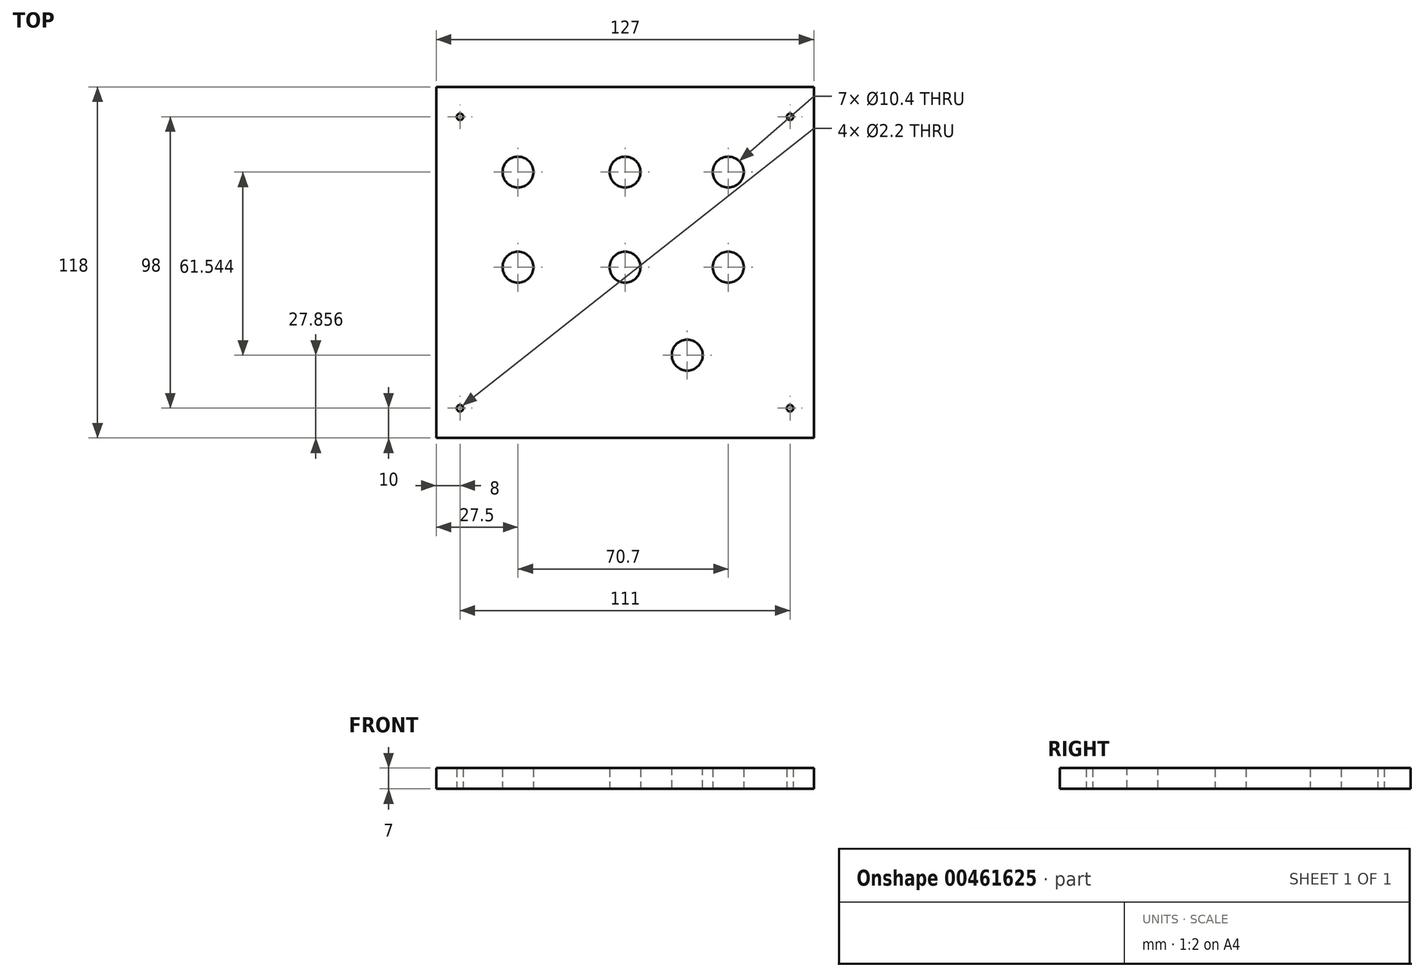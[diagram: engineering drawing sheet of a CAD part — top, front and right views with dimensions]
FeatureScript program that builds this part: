
annotation { "Feature Type Name" : "Feature", "Feature Type Description" : "" }
export const myFeature = defineFeature(function(context is Context, id is Id, definition is map)
    precondition{}
    {
        {
            var Q0;
            Q0=qCreatedBy(makeId("Top.planeOp"),FACE);
            var sketch = newSketch(context, id + "F0", { "sketchPlane" : qUnion([Q0])});
            skLineSegment(sketch, "E0.bottom", {"start": v(-63.5, 59) * mm, "end": v(63.5, 59) * mm});
            skLineSegment(sketch, "E0.top", {"start": v(-63.5, -59) * mm, "end": v(63.5, -59) * mm});
            skLineSegment(sketch, "E0.left", {"start": v(-63.5, 59) * mm, "end": v(-63.5, -59) * mm});
            skLineSegment(sketch, "E0.right", {"start": v(63.5, 59) * mm, "end": v(63.5, -59) * mm});
            skPoint(sketch, "E0.middle", {"position": v(0, 0) * mm});
            skSolve(sketch);
        }
        {
            var Q0;
            Q0=makeQuery(id+"F0.imprint","IMPRINT",FACE,{"disambiguationData":[TD([[makeQuery(id+"F0.imprint","IMPRINT",EDGE,{"derivedFrom":sQuery(id+"F0.wireOp",EDGE,"E0.bottom")}),-1.0]])]});
            extrude(context, id + "F1", {"entities" : qUnion([Q0]), "depth" : 7 * mm, "offsetDistance" : 25 * mm});
        }
        {
            var Q0;
            Q0=makeQuery(id+"F1.opExtrude","CAP_FACE",FACE,{"disambiguationData":[OSD([sQuery(id+"F0.wireOp",EDGE,"E0.bottom"),sQuery(id+"F0.wireOp",EDGE,"E0.top"),sQuery(id+"F0.wireOp",EDGE,"E0.left"),sQuery(id+"F0.wireOp",EDGE,"E0.right")])],"isStart":true});
            var sketch = newSketch(context, id + "F2", { "sketchPlane" : qUnion([Q0])});
            skLineSegment(sketch, "E1", {"start": v(-63.5, -59) * mm, "end": v(-55.5, -59) * mm, "construction": true});
            skLineSegment(sketch, "E2", {"start": v(-55.5, -59) * mm, "end": v(-55.5, -49) * mm});
            skCircle(sketch, "E3", {"center": v(-55.5, -49) * mm, "radius": 1.1 * mm});
            skLineSegment(sketch, "E4", {"start": v(0, -59) * mm, "end": v(0, 59) * mm, "construction": true});
            skCircle(sketch, "E5.MirrorC", {"center": v(55.5, -49) * mm, "radius": 1.1 * mm});
            skLineSegment(sketch, "E6", {"start": v(-63.5, 0) * mm, "end": v(63.5, 0) * mm, "construction": true});
            skCircle(sketch, "E7.MirrorC", {"center": v(-55.5, 49) * mm, "radius": 1.1 * mm});
            skCircle(sketch, "E8.MirrorC", {"center": v(55.5, 49) * mm, "radius": 1.1 * mm});
            skSolve(sketch);
        }
        {
            var Q0;
            Q0 = qSketchRegion(id + "F2", true);
            extrude(context, id + "F3", {"entities" : qUnion([Q0]), "operationType" : NewBodyOperationType.REMOVE, "oppositeDirection" : true, "depth" : 25 * mm, "offsetDistance" : 25 * mm});
        }
        {
            var Q0;
            Q0=qCreatedBy(makeId("Top.planeOp"),FACE);
            var sketch = newSketch(context, id + "F4", { "sketchPlane" : qUnion([Q0])});
            skLineSegment(sketch, "E9", {"start": v(0, 59) * mm, "end": v(0, 30.4) * mm, "construction": true});
            skLineSegment(sketch, "E10", {"start": v(0, 30.4) * mm, "end": v(-36, 30.4) * mm, "construction": true});
            skLineSegment(sketch, "E11", {"start": v(0, 30.4) * mm, "end": v(34.7, 30.4) * mm, "construction": true});
            skLineSegment(sketch, "E12", {"start": v(0, 30.4) * mm, "end": v(0, -1.6) * mm, "construction": true});
            skLineSegment(sketch, "E13", {"start": v(-36, 30.4) * mm, "end": v(-36, -1.6) * mm, "construction": true});
            skLineSegment(sketch, "E14", {"start": v(34.7, 30.4) * mm, "end": v(34.7, -1.6) * mm, "construction": true});
            skCircle(sketch, "E15", {"center": v(-36, 30.4) * mm, "radius": 5.2 * mm});
            skCircle(sketch, "E16", {"center": v(-36, -1.6) * mm, "radius": 5.2 * mm});
            skCircle(sketch, "E17", {"center": v(0, -1.6) * mm, "radius": 5.2 * mm});
            skCircle(sketch, "E18", {"center": v(34.7, -1.6) * mm, "radius": 5.2 * mm});
            skCircle(sketch, "E19", {"center": v(34.7, 30.4) * mm, "radius": 5.2 * mm});
            skCircle(sketch, "E20", {"center": v(0, 30.4) * mm, "radius": 5.2 * mm});
            skSolve(sketch);
        }
        {
            var Q0;
            Q0 = qSketchRegion(id + "F4", true);
            extrude(context, id + "F5", {"entities" : qUnion([Q0]), "operationType" : NewBodyOperationType.REMOVE, "endBound" : BoundingType.THROUGH_ALL, "depth" : 25 * mm, "offsetDistance" : 25 * mm});
        }
        {
            var Q0;
            Q0=makeQuery(id+"F1.opExtrude","CAP_FACE",FACE,{"disambiguationData":[OSD([sQuery(id+"F0.wireOp",EDGE,"E0.bottom"),sQuery(id+"F0.wireOp",EDGE,"E0.top"),sQuery(id+"F0.wireOp",EDGE,"E0.left"),sQuery(id+"F0.wireOp",EDGE,"E0.right")])],"isStart":false});
            var sketch = newSketch(context, id + "F6", { "sketchPlane" : qUnion([Q0])});
            skArc(sketch, "E21", {"start": v(20.92, 27.94) * mm, "mid": v(2.1, -1.6) * mm, "end": v(20.92, -31.14) * mm, "construction": true});
            skArc(sketch, "E22", {"start": v(20.92, -31.14) * mm, "mid": v(36.2, -1.6) * mm, "end": v(20.92, 27.94) * mm, "construction": true});
            skCircle(sketch, "E23", {"center": v(20.92, -31.14) * mm, "radius": 5.2 * mm});
            skSolve(sketch);
        }
        {
            var Q0;
            Q0=makeQuery(id+"F6.imprint","IMPRINT",FACE,{"disambiguationData":[TD([[makeQuery(id+"F6.imprint","IMPRINT",EDGE,{"derivedFrom":sQuery(id+"F6.wireOp",EDGE,"E23")}),1.0]])]});
            extrude(context, id + "F7", {"entities" : qUnion([Q0]), "operationType" : NewBodyOperationType.REMOVE, "endBound" : BoundingType.THROUGH_ALL, "oppositeDirection" : true, "depth" : 25 * mm, "offsetDistance" : 25 * mm});
        }
    });
